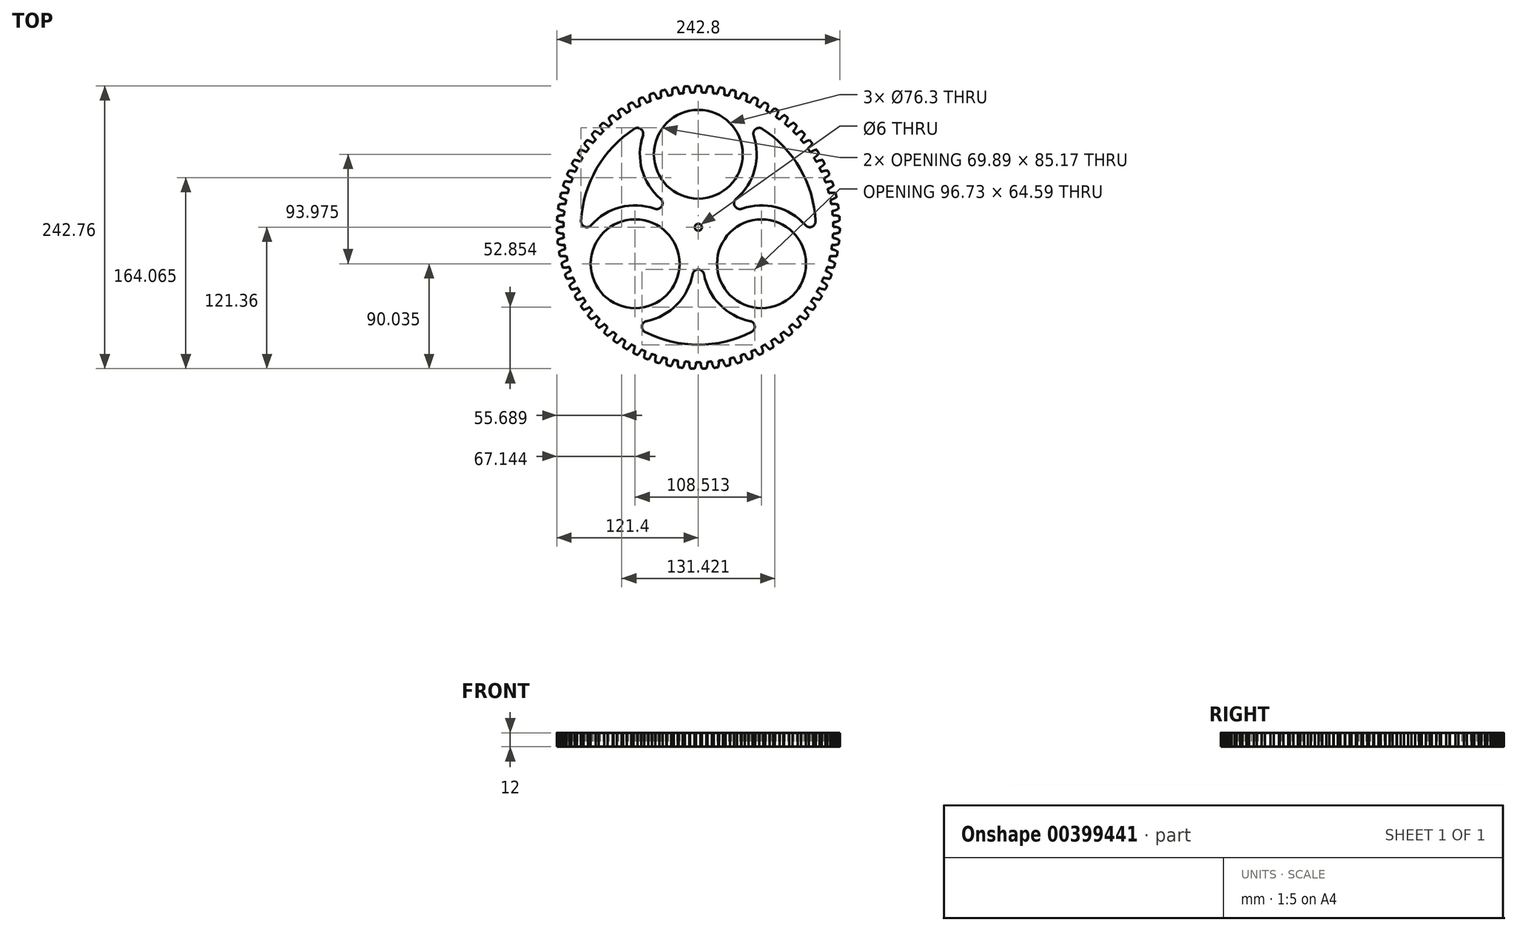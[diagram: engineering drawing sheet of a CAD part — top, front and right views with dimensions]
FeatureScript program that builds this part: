
annotation { "Feature Type Name" : "Feature", "Feature Type Description" : "" }
export const myFeature = defineFeature(function(context is Context, id is Id, definition is map)
    precondition{}
    {
        {
            var Q0;
            Q0=qCreatedBy(makeId("Top.planeOp"),FACE);
            var sketch = newSketch(context, id + "F0", { "sketchPlane" : qUnion([Q0])});
            skCircle(sketch, "E0", {"center": v(0, 0) * mm, "radius": 119 * mm, "construction": true});
            skCircle(sketch, "E1", {"center": v(0, 0) * mm, "radius": 107.5 * mm, "construction": true});
            skCircle(sketch, "E2", {"center": v(0, 0) * mm, "radius": 115.8 * mm, "construction": true});
            skCircle(sketch, "E3", {"center": v(0, 0) * mm, "radius": 121.4 * mm, "construction": true});
            skLineSegment(sketch, "E4", {"start": v(0, 0) * mm, "end": v(2.5, 118.97) * mm, "construction": true});
            skFitSpline(sketch, "E5", {"points": [v(1.87, 121.39) * mm, v(2.92, 115.76) * mm], "startDerivative": vector(2.44, -8.2) * mm, "endDerivative": vector(0.04, -2.85) * mm});
            skLineSegment(sketch, "E6", {"start": v(-33.06, 110.98) * mm, "end": v(1.87, 121.39) * mm, "construction": true});
            skLineSegment(sketch, "E7", {"start": v(1.84, 121.48) * mm, "end": v(1.9, 121.29) * mm, "construction": true});
            skLineSegment(sketch, "E8", {"start": v(2.47, 119.07) * mm, "end": v(2.51, 118.88) * mm, "construction": true});
            skLineSegment(sketch, "E9", {"start": v(2.7, 117.87) * mm, "end": v(2.74, 117.67) * mm, "construction": true});
            skLineSegment(sketch, "E10", {"start": v(-24.3, 113.22) * mm, "end": v(2.5, 118.97) * mm, "construction": true});
            skLineSegment(sketch, "E11", {"start": v(-18.61, 114.3) * mm, "end": v(2.72, 117.77) * mm, "construction": true});
            skLineSegment(sketch, "E12", {"start": v(-29.85, 111.89) * mm, "end": v(2.14, 120.42) * mm, "construction": true});
            skLineSegment(sketch, "E13", {"start": v(2.12, 120.52) * mm, "end": v(2.17, 120.33) * mm, "construction": true});
            skLineSegment(sketch, "E14", {"start": v(-26.26, 112.78) * mm, "end": v(2.38, 119.45) * mm, "construction": true});
            skLineSegment(sketch, "E15", {"start": v(2.36, 119.55) * mm, "end": v(2.4, 119.36) * mm, "construction": true});
            skLineSegment(sketch, "E16", {"start": v(-12.33, 115.14) * mm, "end": v(2.86, 116.77) * mm, "construction": true});
            skLineSegment(sketch, "E17", {"start": v(2.85, 116.87) * mm, "end": v(2.87, 116.67) * mm, "construction": true});
            skArc(sketch, "E18", {"start": v(1.87, 121.39) * mm, "mid": v(0.94, 121.4) * mm, "end": v(0, 121.4) * mm});
            skSolve(sketch);
        }
        {
            var Q0;
            Q0=qCreatedBy(makeId("Top.planeOp"),FACE);
            var sketch = newSketch(context, id + "F1", { "sketchPlane" : qUnion([Q0])});
            skArc(sketch, "E19.0", {"start": v(-2.92, 115.76) * mm, "mid": v(0, -115.8) * mm, "end": v(2.92, 115.76) * mm});
            skCircle(sketch, "E20", {"center": v(0, 0) * mm, "radius": 3 * mm});
            skArc(sketch, "E21.0", {"start": v(1.87, 121.39) * mm, "mid": v(0.94, 121.4) * mm, "end": v(0, 121.4) * mm});
            skFitSpline(sketch, "E22.0", {"points": [v(1.87, 121.39) * mm, v(2.69, 118.65) * mm, v(2.91, 116.71) * mm, v(2.92, 115.76) * mm]});
            skArc(sketch, "E23.MirrorCS", {"start": v(-1.87, 121.39) * mm, "mid": v(-0.94, 121.4) * mm, "end": v(0, 121.4) * mm});
            skFitSpline(sketch, "E24.MirrorCS", {"points": [v(-1.87, 121.39) * mm, v(-2.69, 118.65) * mm, v(-2.91, 116.71) * mm, v(-2.92, 115.76) * mm]});
            skSolve(sketch);
        }
        {
            var Q0;
            Q0 = qSketchRegion(id + "F1", true);
            extrude(context, id + "F2", {"entities" : qUnion([Q0]), "depth" : 12 * mm});
        }
        {
            var Q0;
            Q0=makeQuery(id+"F2.opExtrude","SWEPT_BODY",BODY,{"disambiguationData":[OSD([sQuery(id+"F1.wireOp",EDGE,"eeb95daa-9a2c-4d3b-b40b-bc04c77fced4.1"),sQuery(id+"F1.wireOp",EDGE,"89ce5ca7-42de-484d-9174-436fac9ca7f20.MirrorCS"),sQuery(id+"F1.wireOp",EDGE,"E19.0"),sQuery(id+"F1.wireOp",EDGE,"E20"),sQuery(id+"F1.wireOp",EDGE,"5248a19e-9ef0-46ba-9073-8b5a409f4121.0"),sQuery(id+"F1.wireOp",EDGE,"a3f9b43a-bdc4-48c8-ab19-a17a6acebfe10.MirrorCS")])]});
            var Q1;
            Q1=makeQuery(id+"F2.opExtrude","SWEPT_FACE",FACE,{"disambiguationData":[OSD([sQuery(id+"F1.wireOp",EDGE,"E20")])]});
            circularPattern(context, id + "F3", {"operationType" : NewBodyOperationType.ADD, "entities" : qUnion([Q0]), "axis" : qUnion([Q1]), "angle" : 360 * degree, "instanceCount" : 75, "equalSpace" : true});
        }
        {
            var Q0;
            Q0=qCreatedBy(makeId("Top.planeOp"),FACE);
            var sketch = newSketch(context, id + "F4", { "sketchPlane" : qUnion([Q0])});
            skArc(sketch, "E25", {"start": v(-45.68, -89.86) * mm, "mid": v(0, -100.8) * mm, "end": v(45.68, -89.86) * mm});
            skCircle(sketch, "E26", {"center": v(0, 0) * mm, "radius": 12.5 * mm, "construction": true});
            skCircle(sketch, "E27", {"center": v(0, 62.65) * mm, "radius": 38.15 * mm});
            skCircle(sketch, "E28", {"center": v(54.26, -31.33) * mm, "radius": 38.15 * mm});
            skCircle(sketch, "E29", {"center": v(-54.26, -31.32) * mm, "radius": 38.15 * mm});
            skArc(sketch, "E30", {"start": v(-44.4, -80.5) * mm, "mid": v(-18.48, -66.47) * mm, "end": v(-4.92, -40.32) * mm});
            skArc(sketch, "E31", {"start": v(-47.51, 78.7) * mm, "mid": v(-48.32, 49.24) * mm, "end": v(-32.45, 24.42) * mm});
            skArc(sketch, "E32", {"start": v(91.9, 1.8) * mm, "mid": v(66.8, 17.23) * mm, "end": v(37.37, 15.9) * mm});
            skLineSegment(sketch, "E33", {"start": v(0, 62.65) * mm, "end": v(-54.26, -31.32) * mm, "construction": true});
            skLineSegment(sketch, "E34", {"start": v(54.26, -31.33) * mm, "end": v(0, 62.65) * mm, "construction": true});
            skLineSegment(sketch, "E35", {"start": v(-54.26, -31.32) * mm, "end": v(54.26, -31.33) * mm, "construction": true});
            skArc(sketch, "E36.trimOffspring", {"start": v(100.66, 5.37) * mm, "mid": v(87.3, 50.4) * mm, "end": v(54.98, 84.49) * mm});
            skArc(sketch, "E37.trimOffspring", {"start": v(-54.98, 84.49) * mm, "mid": v(-87.3, 50.4) * mm, "end": v(-100.66, 5.37) * mm});
            skPoint(sketch, "E38.visualSharp", {"position": v(-40.41, 92.34) * mm});
            skArc(sketch, "E38.filletArc", {"start": v(-47.51, 78.7) * mm, "mid": v(-49.19, 84.25) * mm, "end": v(-54.98, 84.49) * mm});
            skPoint(sketch, "E39.visualSharp", {"position": v(-100.18, -11.17) * mm});
            skArc(sketch, "E39.filletArc", {"start": v(-100.66, 5.37) * mm, "mid": v(-97.55, 0.47) * mm, "end": v(-91.9, 1.8) * mm});
            skPoint(sketch, "E40.visualSharp", {"position": v(-59.76, -81.17) * mm});
            skArc(sketch, "E40.filletArc", {"start": v(-44.4, -80.5) * mm, "mid": v(-48.37, -84.72) * mm, "end": v(-45.68, -89.86) * mm});
            skPoint(sketch, "E41.visualSharp", {"position": v(59.76, -81.17) * mm});
            skArc(sketch, "E41.filletArc", {"start": v(45.68, -89.86) * mm, "mid": v(48.37, -84.72) * mm, "end": v(44.4, -80.5) * mm});
            skPoint(sketch, "E42.visualSharp", {"position": v(100.18, -11.17) * mm});
            skArc(sketch, "E42.filletArc", {"start": v(91.9, 1.8) * mm, "mid": v(97.55, 0.47) * mm, "end": v(100.66, 5.37) * mm});
            skPoint(sketch, "E43.visualSharp", {"position": v(40.41, 92.34) * mm});
            skArc(sketch, "E43.filletArc", {"start": v(54.98, 84.49) * mm, "mid": v(49.19, 84.25) * mm, "end": v(47.51, 78.7) * mm});
            skArc(sketch, "E44.trimOffspring", {"start": v(32.45, 24.42) * mm, "mid": v(48.32, 49.24) * mm, "end": v(47.51, 78.7) * mm});
            skArc(sketch, "E45.trimOffspring", {"start": v(4.92, -40.32) * mm, "mid": v(18.48, -66.47) * mm, "end": v(44.4, -80.5) * mm});
            skArc(sketch, "E46.trimOffspring", {"start": v(-37.37, 15.9) * mm, "mid": v(-66.8, 17.23) * mm, "end": v(-91.9, 1.8) * mm});
            skArc(sketch, "E47.filletArc", {"start": v(32.45, 24.42) * mm, "mid": v(31.36, 18.1) * mm, "end": v(37.37, 15.9) * mm});
            skArc(sketch, "E48.filletArc", {"start": v(-37.37, 15.9) * mm, "mid": v(-31.36, 18.1) * mm, "end": v(-32.45, 24.42) * mm});
            skArc(sketch, "E49.filletArc", {"start": v(4.92, -40.32) * mm, "mid": v(0, -36.21) * mm, "end": v(-4.92, -40.32) * mm});
            skSolve(sketch);
        }
        {
            var Q0;
            Q0 = qSketchRegion(id + "F4", true);
            extrude(context, id + "F5", {"entities" : qUnion([Q0]), "operationType" : NewBodyOperationType.REMOVE, "endBound" : BoundingType.THROUGH_ALL, "depth" : 25 * mm});
        }
    });
